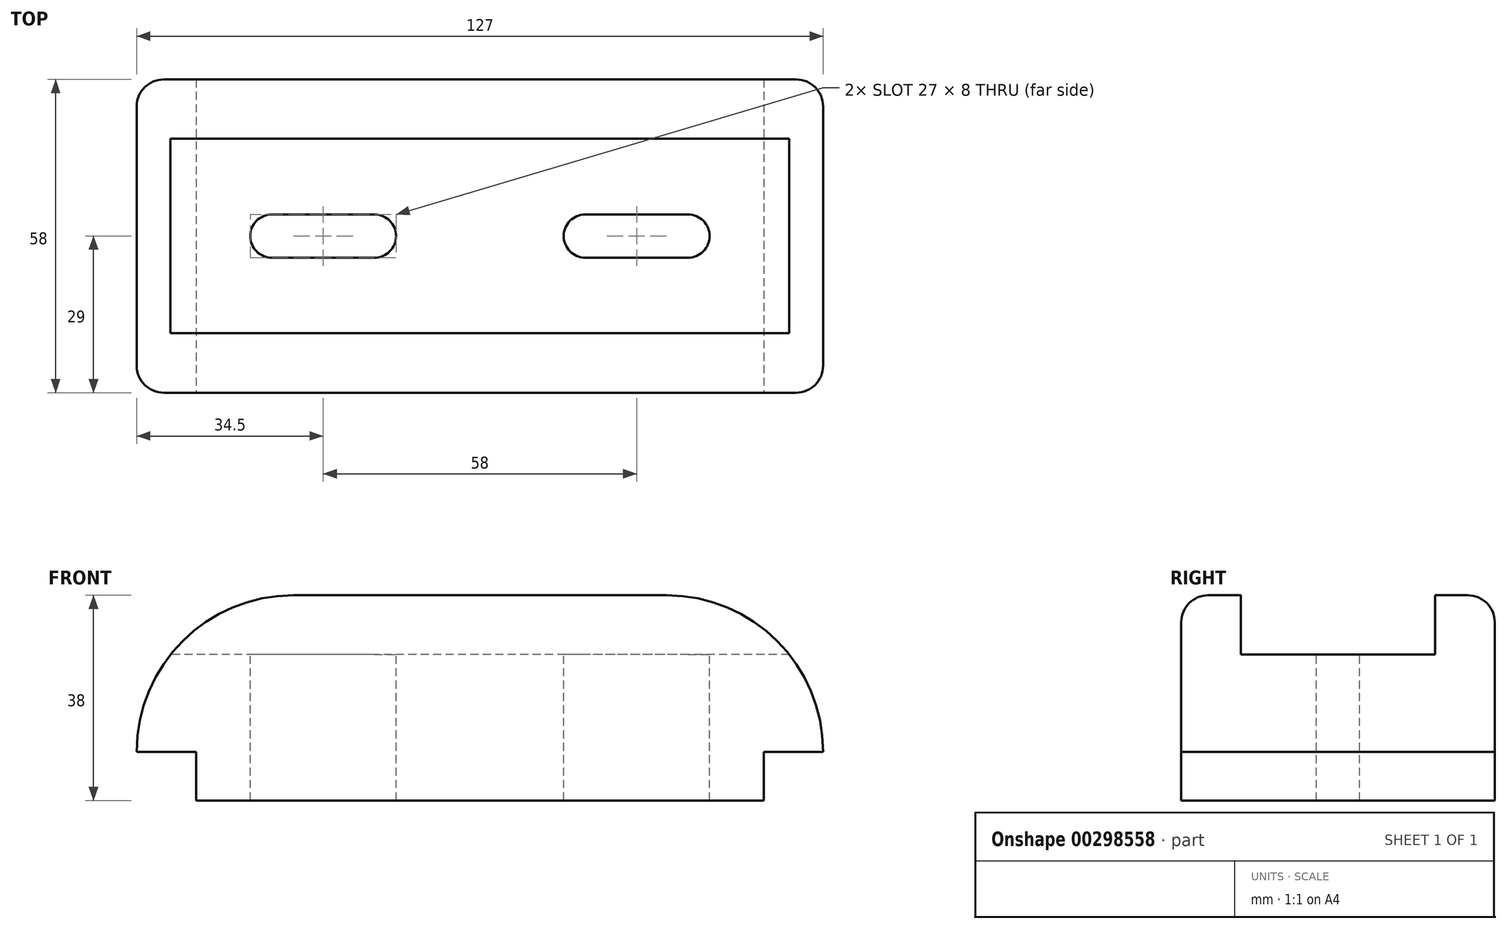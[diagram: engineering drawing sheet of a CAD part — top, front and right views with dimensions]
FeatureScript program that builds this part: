
annotation { "Feature Type Name" : "Feature", "Feature Type Description" : "" }
export const myFeature = defineFeature(function(context is Context, id is Id, definition is map)
    precondition{}
    {
        {
            var Q0;
            Q0=qCreatedBy(makeId("Front.planeOp"),FACE);
            var sketch = newSketch(context, id + "F0", { "sketchPlane" : qUnion([Q0])});
            skLineSegment(sketch, "E0.bottom", {"start": v(0, 0) * mm, "end": v(127, 0) * mm});
            skLineSegment(sketch, "E0.top", {"start": v(29, 38) * mm, "end": v(98, 38) * mm});
            skLineSegment(sketch, "E0.left", {"start": v(0, 0) * mm, "end": v(0, 9) * mm});
            skLineSegment(sketch, "E0.right", {"start": v(127, 0) * mm, "end": v(127, 9) * mm});
            skPoint(sketch, "E1.visualSharp", {"position": v(0, 38) * mm});
            skArc(sketch, "E1.filletArc", {"start": v(29, 38) * mm, "mid": v(8.5, 29.5) * mm, "end": v(0, 9) * mm});
            skPoint(sketch, "E2.visualSharp", {"position": v(127, 38) * mm});
            skArc(sketch, "E2.filletArc", {"start": v(127, 9) * mm, "mid": v(118.5, 29.5) * mm, "end": v(98, 38) * mm});
            skSolve(sketch);
        }
        {
            var Q0;
            Q0 = qSketchRegion(id + "F0", true);
            extrude(context, id + "F1", {"entities" : qUnion([Q0]), "depth" : 58 * mm});
        }
        {
            var Q0;
            Q0=makeQuery(id+"F1.opExtrude","CAP_FACE",FACE,{"disambiguationData":[OSD([sQuery(id+"F0.wireOp",EDGE,"E0.bottom"),sQuery(id+"F0.wireOp",EDGE,"E0.top"),sQuery(id+"F0.wireOp",EDGE,"E0.left"),sQuery(id+"F0.wireOp",EDGE,"E0.right"),sQuery(id+"F0.wireOp",EDGE,"E1.filletArc"),sQuery(id+"F0.wireOp",EDGE,"E2.filletArc")])],"isStart":false});
            var sketch = newSketch(context, id + "F2", { "sketchPlane" : qUnion([Q0])});
            skLineSegment(sketch, "E3.bottom", {"start": v(0, 0) * mm, "end": v(11, 0) * mm});
            skLineSegment(sketch, "E3.top", {"start": v(0, 9) * mm, "end": v(11, 9) * mm});
            skLineSegment(sketch, "E3.left", {"start": v(0, 0) * mm, "end": v(0, 9) * mm});
            skLineSegment(sketch, "E3.right", {"start": v(11, 0) * mm, "end": v(11, 9) * mm});
            skLineSegment(sketch, "E4.bottom", {"start": v(127, 0) * mm, "end": v(116, 0) * mm});
            skLineSegment(sketch, "E4.top", {"start": v(127, 9) * mm, "end": v(116, 9) * mm});
            skLineSegment(sketch, "E4.left", {"start": v(127, 0) * mm, "end": v(127, 9) * mm});
            skLineSegment(sketch, "E4.right", {"start": v(116, 0) * mm, "end": v(116, 9) * mm});
            skSolve(sketch);
        }
        {
            var Q0;
            Q0 = qSketchRegion(id + "F2", true);
            extrude(context, id + "F3", {"entities" : qUnion([Q0]), "operationType" : NewBodyOperationType.REMOVE, "endBound" : BoundingType.THROUGH_ALL, "oppositeDirection" : true, "depth" : 25 * mm});
        }
        {
            var Q0;
            Q0=qCreatedBy(makeId("Right.planeOp"),FACE);
            var sketch = newSketch(context, id + "F4", { "sketchPlane" : qUnion([Q0])});
            skLineSegment(sketch, "E5.bottom", {"start": v(-47, 38) * mm, "end": v(-11, 38) * mm});
            skLineSegment(sketch, "E5.top", {"start": v(-47, 27) * mm, "end": v(-11, 27) * mm});
            skLineSegment(sketch, "E5.left", {"start": v(-47, 38) * mm, "end": v(-47, 27) * mm});
            skLineSegment(sketch, "E5.right", {"start": v(-11, 38) * mm, "end": v(-11, 27) * mm});
            skSolve(sketch);
        }
        {
            var Q0;
            Q0 = qSketchRegion(id + "F4", true);
            extrude(context, id + "F5", {"entities" : qUnion([Q0]), "operationType" : NewBodyOperationType.REMOVE, "endBound" : BoundingType.THROUGH_ALL, "depth" : 25 * mm});
        }
        {
            var Q0;
            Q0=makeQuery(id+"F5.boolean.opBoolean","COPY",FACE,{"derivedFrom":makeQuery(id+"F5.opExtrude","SWEPT_FACE",FACE,{"disambiguationData":[OSD([sQuery(id+"F4.wireOp",EDGE,"E5.top")])]})});
            var sketch = newSketch(context, id + "F6", { "sketchPlane" : qUnion([Q0])});
            skArc(sketch, "E6", {"start": v(25, -25) * mm, "mid": v(21, -29) * mm, "end": v(25, -33) * mm});
            skArc(sketch, "E7", {"start": v(44, -33) * mm, "mid": v(48, -29) * mm, "end": v(44, -25) * mm});
            skArc(sketch, "E8", {"start": v(83, -25) * mm, "mid": v(79, -29) * mm, "end": v(83, -33) * mm});
            skArc(sketch, "E9", {"start": v(102, -33) * mm, "mid": v(106, -29) * mm, "end": v(102, -25) * mm});
            skLineSegment(sketch, "E10", {"start": v(44, -25) * mm, "end": v(25, -25) * mm});
            skLineSegment(sketch, "E11", {"start": v(44, -33) * mm, "end": v(25, -33) * mm});
            skLineSegment(sketch, "E12", {"start": v(83, -33) * mm, "end": v(102, -33) * mm});
            skLineSegment(sketch, "E13", {"start": v(102, -25) * mm, "end": v(83, -25) * mm});
            skSolve(sketch);
        }
        {
            var Q0;
            Q0 = qSketchRegion(id + "F6", true);
            extrude(context, id + "F7", {"entities" : qUnion([Q0]), "operationType" : NewBodyOperationType.REMOVE, "endBound" : BoundingType.THROUGH_ALL, "oppositeDirection" : true, "depth" : 25 * mm});
        }
        {
            var Q0;
            Q0=makeQuery(id+"F1.opExtrude","CAP_EDGE",EDGE,{"disambiguationData":[OSD([sQuery(id+"F0.wireOp",EDGE,"E0.top")])],"isStart":false});
            var Q1;
            Q1=makeQuery(id+"F1.opExtrude","CAP_EDGE",EDGE,{"disambiguationData":[OSD([sQuery(id+"F0.wireOp",EDGE,"E0.top")])],"isStart":true});
            fillet(context, id + "F8", {"entities" : qUnion([Q0, Q1]), "radius" : 5 * mm, "tangentPropagation" : true, "allowEdgeOverflow" : false});
        }
    });
